# Revit family: PRD_FrankeWS_ShwrHds_EmergencyShowerhead_FAID0001
name_source: partatom
category: Plumbing Fixtures
revit_build: Autodesk Revit 2018 (Build: 20190510_1515(x64)
units: mm (PartAtom-declared; Revit-internal decimal feet)

## family parameters
Always vertical = Yes
Cut with Voids When Loaded = No
OmniClass Number = 23.45.05.14.99
OmniClass Title = Other Sanitary Washing Plumbing Fixtures
Part Type = Normal
Room Calculation Point = No
Round Connector Dimension = Use Diameter
Shared = No
Work Plane-Based = Yes

## types (1)
- FAID0001
    AssetType = Fixed
    BIMObjectName = PRD_AR_ShowerHeads_EmergencyShowerhead_FAID0001
    Category = Pr_40_20_87_76, Shower heads
    Color = green
    Default Elevation = 0 mm  [stored 0 ft]
    Description = Emergency shower head DN 20, self-draining, green EPS coated brass (RAL 6032). Complies with EN 15154, Part 1. Volumetric flow rate approx. 65 l/min at 1 bar pressure, volumetric flow rate approx. 110 l/min at 3 bar pressure.
    DiameterNominal = 20 mm
    DrainSize = 20 mm  [stored 0.0656168 ft]
    DurationUnit = year
    Features = DN 20, self-draining
    Finish = EPS coated
    FittingMaterial = PRD_AR_Brass_EPSCoated_Green
    GrossWeight = 0.4 kg
    HasTray = FALSE
    IfcExportAs = IfcSanitaryTerminalType
    IfcExportType = SHOWER
    InletSize = DN-20-3-4INH
    Manufacturer = KWC Group AG
    ManufacturerName = KWC Group AG
    ManufacturerURL = www.kwc.com
    Material = brass
    Model = FAID0001
    ModelNumber = 2030018810
    ModelReference = FAID0001
    NBSDescription = Shower heads
    NBSReference = 45-35-70/333
    Name = Emergency Showerhead FAID0001
    NetWeight = 0.4 kg
    NominalDepth = 40 mm  [stored 0.131234 ft]
    NominalHeight = 62 mm  [stored 0.203412 ft]
    NominalWidth = 40 mm  [stored 0.131234 ft]
    ProductInformation = https://pim.kwc.com
    ShowerHeadDescription = Emergency shower head
    ShowerType = Individual
    Size = 40 x 62 x 40 mm (W x H x D)
    Type = EMERG-SHOWER-HEAD
    TypeOfFitting = Cantilever connection
    URL = www.kwc.com
    Uniclass2015Code = Pr_40_20_87_76
    Uniclass2015Title = Shower heads
    Uniclass2015Version = Products v1.17
    Version = 1
    VolumeFlowRate = 1.83 l/s at 3 bar
    WarrantyDurationUnit = year

note: [stored X ft] marks values corroborated as IEEE doubles in the binary element streams (Revit-internal decimal feet)

## geometry (parser evidence)
native form markers: Sweep x3
no freeform markers — native parametric forms only
